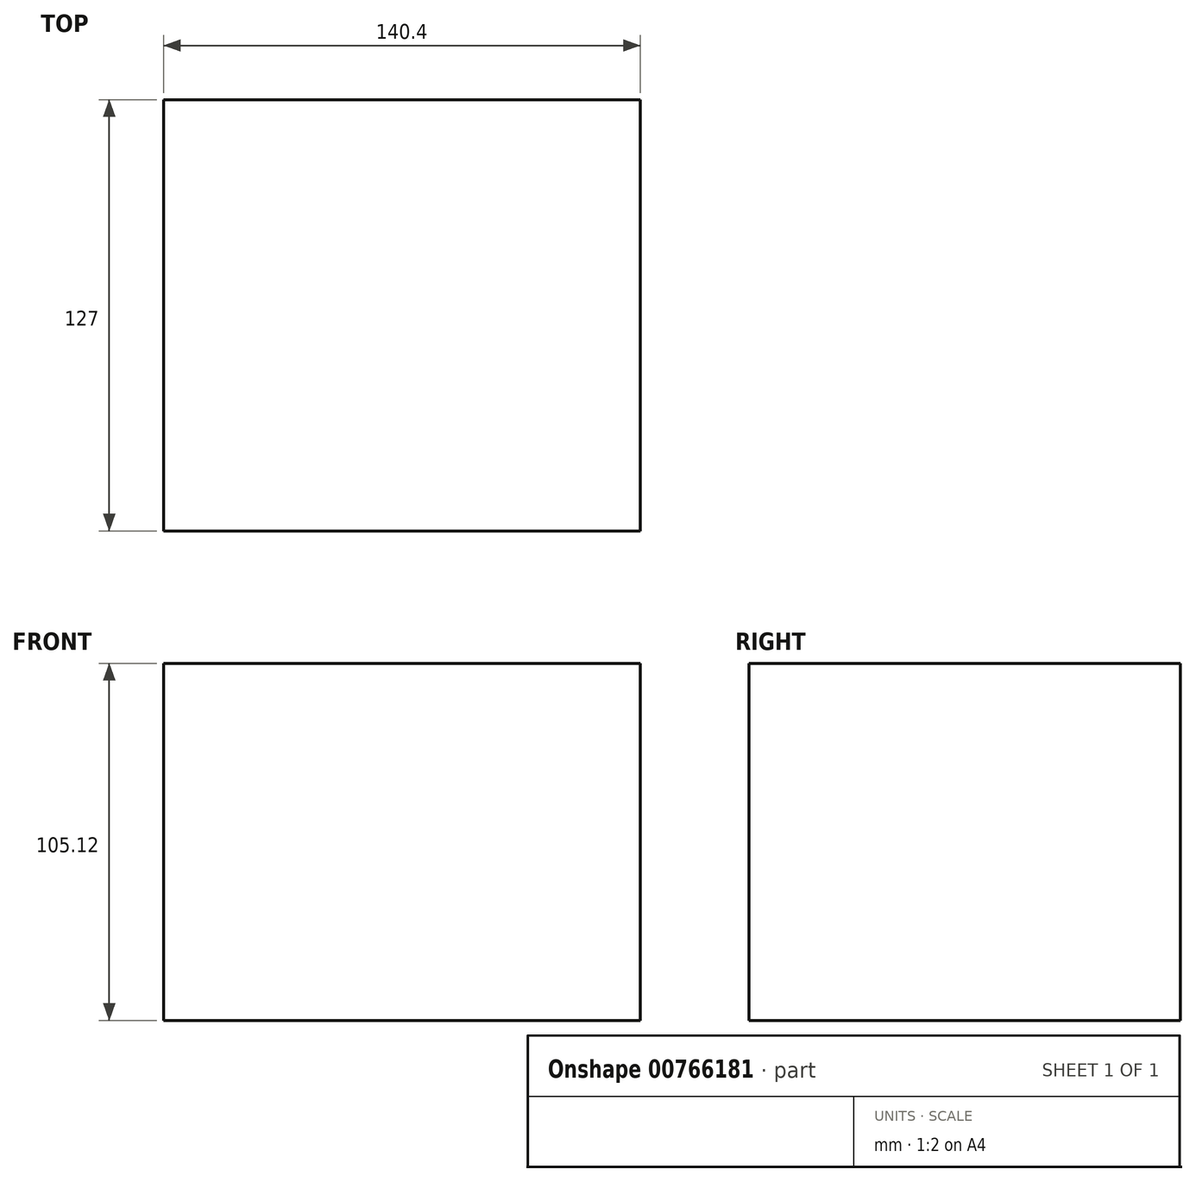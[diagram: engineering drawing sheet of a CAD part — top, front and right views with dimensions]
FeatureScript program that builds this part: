
annotation { "Feature Type Name" : "Feature", "Feature Type Description" : "" }
export const myFeature = defineFeature(function(context is Context, id is Id, definition is map)
    precondition{}
    {
        {
            var Q0;
            Q0=qCreatedBy(makeId("Front.planeOp"),FACE);
            var sketch = newSketch(context, id + "F0", { "sketchPlane" : qUnion([Q0])});
            skLineSegment(sketch, "E0.bottom", {"start": v(-63.31, -20.6) * mm, "end": v(77.1, -20.6) * mm});
            skLineSegment(sketch, "E0.top", {"start": v(-63.31, 84.5) * mm, "end": v(77.1, 84.5) * mm});
            skLineSegment(sketch, "E0.left", {"start": v(-63.31, -20.6) * mm, "end": v(-63.31, 84.5) * mm});
            skLineSegment(sketch, "E0.right", {"start": v(77.1, -20.6) * mm, "end": v(77.1, 84.5) * mm});
            skPoint(sketch, "E0.middle", {"position": v(6.9, 31.95) * mm});
            skSolve(sketch);
        }
        {
            var Q0;
            Q0=makeQuery(id+"F0.imprint","IMPRINT",FACE,{"disambiguationData":[TD([[makeQuery(id+"F0.imprint","IMPRINT",EDGE,{"derivedFrom":sQuery(id+"F0.wireOp",EDGE,"E0.bottom")}),1.0]])]});
            extrude(context, id + "F1", {"entities" : qUnion([Q0]), "depth" : 127 * mm, "offsetDistance" : 25.4 * mm});
        }
    });
